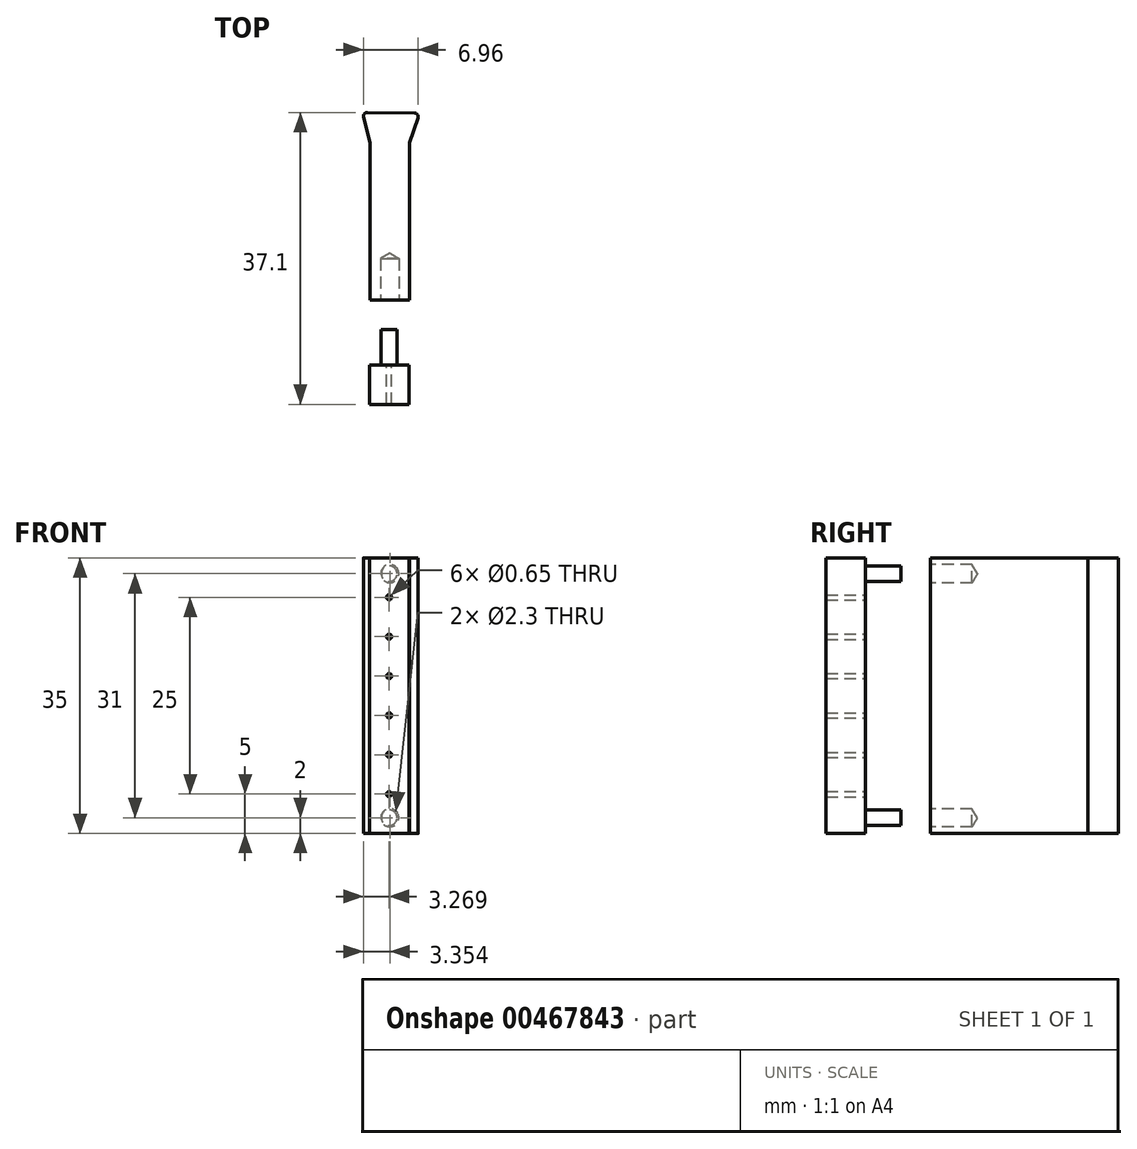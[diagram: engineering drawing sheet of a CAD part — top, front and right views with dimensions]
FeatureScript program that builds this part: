
annotation { "Feature Type Name" : "Feature", "Feature Type Description" : "" }
export const myFeature = defineFeature(function(context is Context, id is Id, definition is map)
    precondition{}
    {
        {
            var Q0;
            Q0=qCreatedBy(makeId("Top.planeOp"),FACE);
            var sketch = newSketch(context, id + "F0", { "sketchPlane" : qUnion([Q0])});
            skLineSegment(sketch, "E0", {"start": v(-47.87, 30.28) * mm, "end": v(-42.87, 30.28) * mm});
            skLineSegment(sketch, "E1", {"start": v(-47.87, 30.28) * mm, "end": v(-47.87, 10.28) * mm});
            skLineSegment(sketch, "E2", {"start": v(-42.87, 30.28) * mm, "end": v(-42.87, 10.28) * mm});
            skLineSegment(sketch, "E3", {"start": v(-47.87, 10.28) * mm, "end": v(-42.87, 10.28) * mm});
            skLineSegment(sketch, "E4", {"start": v(-47.87, 34.14) * mm, "end": v(-48.21, 34.14) * mm});
            skLineSegment(sketch, "E5", {"start": v(-48.62, 33.18) * mm, "end": v(-48.7, 33.52) * mm});
            skArc(sketch, "E6.filletArc", {"start": v(-48.21, 34.14) * mm, "mid": v(-48.61, 33.95) * mm, "end": v(-48.7, 33.52) * mm});
            skLineSegment(sketch, "E7", {"start": v(-42.26, 34.07) * mm, "end": v(-42.57, 34.07) * mm});
            skLineSegment(sketch, "E8", {"start": v(-41.8, 33.4) * mm, "end": v(-41.9, 33.11) * mm});
            skArc(sketch, "E9.filletArc", {"start": v(-41.8, 33.4) * mm, "mid": v(-41.86, 33.86) * mm, "end": v(-42.26, 34.07) * mm});
            skLineSegment(sketch, "E10", {"start": v(-48.62, 33.18) * mm, "end": v(-47.87, 30.28) * mm});
            skLineSegment(sketch, "E11", {"start": v(-42.87, 30.28) * mm, "end": v(-41.9, 33.11) * mm});
            skLineSegment(sketch, "E12", {"start": v(-42.57, 34.07) * mm, "end": v(-47.87, 34.14) * mm});
            skSolve(sketch);
        }
        {
            var Q0;
            Q0 = qSketchRegion(id + "F0", true);
            extrude(context, id + "F1", {"entities" : qUnion([Q0]), "depth" : 35 * mm});
        }
        {
            var Q0;
            Q0=makeQuery(id+"F1.opExtrude","SWEPT_FACE",FACE,{"disambiguationData":[OSD([sQuery(id+"F0.wireOp",EDGE,"E3")])]});
            var sketch = newSketch(context, id + "F2", { "sketchPlane" : qUnion([Q0])});
            skCircle(sketch, "E13", {"center": v(-45.37, 33) * mm, "radius": 1 * mm});
            skCircle(sketch, "E14", {"center": v(-45.37, 2) * mm, "radius": 1 * mm});
            skSolve(sketch);
        }
        {
            var Q0;
            Q0=sQuery(id+"F2.wireOp",VERTEX,"E14.center");
            var Q1;
            Q1=sQuery(id+"F2.wireOp",VERTEX,"E13.center");
            var Q2;
            Q2=makeQuery(id+"F1.opExtrude","SWEPT_BODY",BODY,{"disambiguationData":[OSD([sQuery(id+"F0.wireOp",EDGE,"E1"),sQuery(id+"F0.wireOp",EDGE,"E2"),sQuery(id+"F0.wireOp",EDGE,"E3"),sQuery(id+"F0.wireOp",EDGE,"E4"),sQuery(id+"F0.wireOp",EDGE,"E5"),sQuery(id+"F0.wireOp",EDGE,"E6.filletArc"),sQuery(id+"F0.wireOp",EDGE,"E7"),sQuery(id+"F0.wireOp",EDGE,"E8"),sQuery(id+"F0.wireOp",EDGE,"E9.filletArc"),sQuery(id+"F0.wireOp",EDGE,"E10"),sQuery(id+"F0.wireOp",EDGE,"E11"),sQuery(id+"F0.wireOp",EDGE,"E12")])]});
            hole(context, id + "F3", {"style" : HoleStyle.SIMPLE, "endStyle" : HoleEndStyle.BLIND, "holeDiameter" : 2.3 * mm, "holeDepth" : 5.3 * mm, "isTappedThrough" : true, "tappedDepth" : 12 * mm, "tapClearance" : 3, "locations" : qUnion([Q0, Q1]), "scope" : qUnion([Q2])});
        }
        {
            var Q0;
            Q0=qCreatedBy(makeId("Top.planeOp"),FACE);
            var sketch = newSketch(context, id + "F4", { "sketchPlane" : qUnion([Q0])});
            skLineSegment(sketch, "E15.bottom", {"start": v(-32.35, 22.04) * mm, "end": v(-27.35, 22.04) * mm});
            skLineSegment(sketch, "E15.top", {"start": v(-32.35, 17.04) * mm, "end": v(-27.35, 17.04) * mm});
            skLineSegment(sketch, "E15.left", {"start": v(-32.35, 22.04) * mm, "end": v(-32.35, 17.04) * mm});
            skLineSegment(sketch, "E15.right", {"start": v(-27.35, 22.04) * mm, "end": v(-27.35, 17.04) * mm});
            skSolve(sketch);
        }
        {
            var Q0;
            Q0=makeQuery(id+"F4.imprint","IMPRINT",FACE,{"disambiguationData":[TD([[makeQuery(id+"F4.imprint","IMPRINT",EDGE,{"derivedFrom":sQuery(id+"F4.wireOp",EDGE,"E15.bottom")}),-1.0]])]});
            extrude(context, id + "F5", {"entities" : qUnion([Q0]), "depth" : 35 * mm});
        }
        {
            var Q0;
            Q0=makeQuery(id+"F5.opExtrude","SWEPT_FACE",FACE,{"disambiguationData":[OSD([sQuery(id+"F4.wireOp",EDGE,"E15.bottom")])]});
            var sketch = newSketch(context, id + "F6", { "sketchPlane" : qUnion([Q0])});
            skCircle(sketch, "E16", {"center": v(29.85, 33) * mm, "radius": 1 * mm});
            skCircle(sketch, "E17", {"center": v(29.85, 2) * mm, "radius": 1 * mm});
            skLineSegment(sketch, "E18", {"start": v(29.85, 33) * mm, "end": v(29.85, 30) * mm});
            skLineSegment(sketch, "E19", {"start": v(29.85, 30) * mm, "end": v(29.85, 25) * mm});
            skLineSegment(sketch, "E20", {"start": v(29.85, 20) * mm, "end": v(29.85, 15) * mm});
            skLineSegment(sketch, "E21", {"start": v(29.85, 25) * mm, "end": v(29.85, 20) * mm});
            skLineSegment(sketch, "E22", {"start": v(29.85, 15) * mm, "end": v(29.85, 10) * mm});
            skLineSegment(sketch, "E23", {"start": v(27.35, 33) * mm, "end": v(29.85, 33) * mm});
            skLineSegment(sketch, "E24", {"start": v(27.35, 2) * mm, "end": v(29.85, 2) * mm});
            skLineSegment(sketch, "E25", {"start": v(29.85, 10) * mm, "end": v(29.85, 5) * mm});
            skLineSegment(sketch, "E26", {"start": v(29.85, 33) * mm, "end": v(29.85, 35) * mm});
            skLineSegment(sketch, "E27", {"start": v(29.85, 2) * mm, "end": v(29.85, 0) * mm});
            skLineSegment(sketch, "E28", {"start": v(29.85, 5) * mm, "end": v(29.85, 2) * mm});
            skCircle(sketch, "E29", {"center": v(29.85, 30) * mm, "radius": 0.33 * mm});
            skCircle(sketch, "E30", {"center": v(29.85, 25) * mm, "radius": 0.33 * mm});
            skCircle(sketch, "E31", {"center": v(29.85, 20) * mm, "radius": 0.33 * mm});
            skCircle(sketch, "E32", {"center": v(29.85, 15) * mm, "radius": 0.33 * mm});
            skCircle(sketch, "E33", {"center": v(29.85, 10) * mm, "radius": 0.33 * mm});
            skCircle(sketch, "E34", {"center": v(29.85, 5) * mm, "radius": 0.33 * mm});
            skSolve(sketch);
        }
        {
            var Q0;
            Q0=makeQuery(id+"F6.imprint","IMPRINT",FACE,{"disambiguationData":[TD([[makeQuery(id+"F6.imprint","IMPRINT",EDGE,{"derivedFrom":sQuery(id+"F6.wireOp",EDGE,"E17")}),1.0]])]});
            extrude(context, id + "F7", {"entities" : qUnion([Q0]), "operationType" : NewBodyOperationType.ADD, "depth" : 4.5 * mm});
        }
        {
            var Q0;
            Q0=makeQuery(id+"F6.imprint","IMPRINT",FACE,{"disambiguationData":[TD([[makeQuery(id+"F6.imprint","IMPRINT",EDGE,{"derivedFrom":sQuery(id+"F6.wireOp",EDGE,"E16")}),1.0]])]});
            extrude(context, id + "F8", {"entities" : qUnion([Q0]), "operationType" : NewBodyOperationType.ADD, "depth" : 4.5 * mm});
        }
        {
            var Q0;
            Q0=sQuery(id+"F6.wireOp",VERTEX,"E29.center");
            var Q1;
            Q1=sQuery(id+"F6.wireOp",VERTEX,"E21.start");
            var Q2;
            Q2=sQuery(id+"F6.wireOp",VERTEX,"E21.end");
            var Q3;
            Q3=sQuery(id+"F6.wireOp",VERTEX,"E22.start");
            var Q4;
            Q4=sQuery(id+"F6.wireOp",VERTEX,"E33.center");
            var Q5;
            Q5=sQuery(id+"F6.wireOp",VERTEX,"E25.end");
            var Q6;
            Q6=makeQuery(id+"F5.opExtrude","SWEPT_BODY",BODY,{"disambiguationData":[OSD([sQuery(id+"F4.wireOp",EDGE,"E15.bottom"),sQuery(id+"F4.wireOp",EDGE,"E15.top"),sQuery(id+"F4.wireOp",EDGE,"E15.left"),sQuery(id+"F4.wireOp",EDGE,"E15.right")])]});
            hole(context, id + "F9", {"style" : HoleStyle.SIMPLE, "endStyle" : HoleEndStyle.THROUGH, "holeDiameter" : .65 * mm, "isTappedThrough" : true, "tappedDepth" : 12 * mm, "tapClearance" : 3, "locations" : qUnion([Q0, Q1, Q2, Q3, Q4, Q5]), "scope" : qUnion([Q6])});
        }
        {
            var Q0;
            Q0=makeQuery(id+"F1.opExtrude","SWEPT_BODY",BODY,{"disambiguationData":[OSD([sQuery(id+"F0.wireOp",EDGE,"E1"),sQuery(id+"F0.wireOp",EDGE,"E2"),sQuery(id+"F0.wireOp",EDGE,"E3"),sQuery(id+"F0.wireOp",EDGE,"E4"),sQuery(id+"F0.wireOp",EDGE,"E5"),sQuery(id+"F0.wireOp",EDGE,"E6.filletArc"),sQuery(id+"F0.wireOp",EDGE,"E7"),sQuery(id+"F0.wireOp",EDGE,"E8"),sQuery(id+"F0.wireOp",EDGE,"E9.filletArc"),sQuery(id+"F0.wireOp",EDGE,"E10"),sQuery(id+"F0.wireOp",EDGE,"E11"),sQuery(id+"F0.wireOp",EDGE,"E12")])]});
            var Q1;
            Q1=makeQuery(id+"F1.opExtrude","CAP_EDGE",EDGE,{"disambiguationData":[OSD([sQuery(id+"F0.wireOp",EDGE,"E3")])],"isStart":false});
            transform(context, id + "F10", {"entities" : qUnion([Q0]), "transformType" : TransformType.TRANSLATION_DISTANCE, "transformDirection" : qUnion([Q1]), "distance" : 15.6 * mm, "makeCopy" : false});
        }
        {
            var Q0;
            Q0=makeQuery(id+"F1.opExtrude","SWEPT_BODY",BODY,{"disambiguationData":[OSD([sQuery(id+"F0.wireOp",EDGE,"E1"),sQuery(id+"F0.wireOp",EDGE,"E2"),sQuery(id+"F0.wireOp",EDGE,"E3"),sQuery(id+"F0.wireOp",EDGE,"E4"),sQuery(id+"F0.wireOp",EDGE,"E5"),sQuery(id+"F0.wireOp",EDGE,"E6.filletArc"),sQuery(id+"F0.wireOp",EDGE,"E7"),sQuery(id+"F0.wireOp",EDGE,"E8"),sQuery(id+"F0.wireOp",EDGE,"E9.filletArc"),sQuery(id+"F0.wireOp",EDGE,"E10"),sQuery(id+"F0.wireOp",EDGE,"E11"),sQuery(id+"F0.wireOp",EDGE,"E12")])]});
            var Q1;
            Q1=makeQuery(id+"F1.opExtrude","CAP_EDGE",EDGE,{"disambiguationData":[OSD([sQuery(id+"F0.wireOp",EDGE,"E2")])],"isStart":false});
            transform(context, id + "F11", {"entities" : qUnion([Q0]), "transformType" : TransformType.TRANSLATION_ENTITY, "oppositeDirectionEntity" : true, "transformLine" : qUnion([Q1]), "makeCopy" : false});
        }
    });
